# Revit family: Electronics_Controls_Biamp_Tesira_Ethernet-Control_TEC-1__
name_source: partatom
category: Communication Devices
units: mm (PartAtom-declared; Revit-internal decimal feet)

## family parameters
Cut with Voids When Loaded = No
Host = Face
Maintain Annotation Orientation = No
OmniClass Number = 23.85.50.17.11.14
OmniClass Title = Network Switchers
Part Type = Normal
Room Calculation Point = No
Round Connector Dimension = Use Diameter
Shared = No

## types (2) — shared parameters
Apparent Load = 0 VA
Compliance = RoHS Directive; CE; FCC
Connector Description = PoE (IEEE 802.3at Class 1, 4W)
Control Cable Length = h 330' (100m) Ethernet cable length can be extended with standard PoE network technology
Control Cable Requirements = Unshielded twisted pair (UTP) wiring, 100BaseT interface (CAT-5/6/7 Ethernet cable) using either RJ-45 or
Insulation Displacement Connector (IDC)
Control Programming = Each control configured for specific operation by the system design software
Control Wiring Topology = Standard Ethernet network wiring
Default Elevation = 4' - 0"
Housing Material = Biamp - Plastic - White
Manufacturer = Biamp
Max Power Consumption = 0 W
Number of Poles = 1
Power Factor = 1
Product Documentation Link = https://downloads.biamp.com
Product Page URL = https://www.biamp.com
Product data url = https://www.bimobject.com
URL = https://www.biamp.com
Voltage = 0 V
Weight = 0.50 lbf

## per-type parameters (varying)
| type | Depth | Description | Height | Model | TEC1i | TEC1s | Width |
| TEC-1s | 0' - 1 1/4" | Tesira® TEC-1s Ethernet Control | 0' - 5 3/32" | Tesira TEC-1s | No | Yes | 0' - 4 11/16" |
| TEC-1i | 0' - 0 1/2" | Tesira® TEC-1i Ethernet Control | 0' - 6 7/32" | Tesira TEC-1i | Yes | No | 0' - 5 13/16" |

## geometry (parser evidence)
native form markers: Sweep x2
no freeform markers — native parametric forms only
